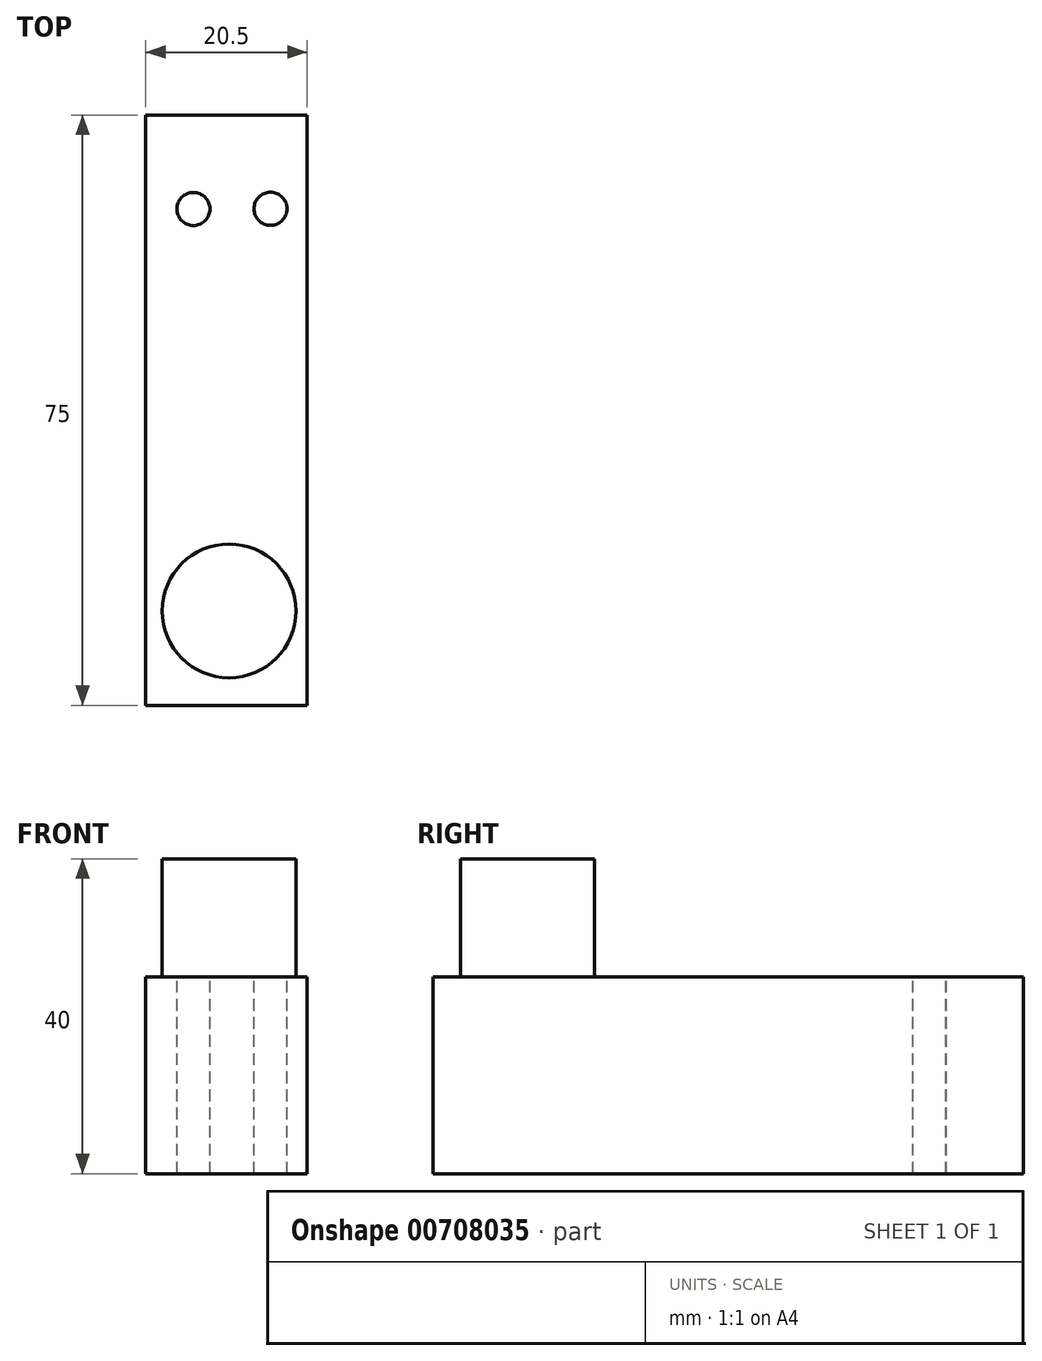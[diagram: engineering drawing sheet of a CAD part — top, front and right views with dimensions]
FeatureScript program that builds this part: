
annotation { "Feature Type Name" : "Feature", "Feature Type Description" : "" }
export const myFeature = defineFeature(function(context is Context, id is Id, definition is map)
    precondition{}
    {
        {
            var Q0;
            Q0=qCreatedBy(makeId("Top.planeOp"),FACE);
            var sketch = newSketch(context, id + "F0", { "sketchPlane" : qUnion([Q0])});
            skLineSegment(sketch, "E0.bottom", {"start": v(-10.6, 51.98) * mm, "end": v(9.9, 51.98) * mm});
            skLineSegment(sketch, "E0.top", {"start": v(-10.6, -23.02) * mm, "end": v(9.9, -23.02) * mm});
            skLineSegment(sketch, "E0.left", {"start": v(-10.6, 51.98) * mm, "end": v(-10.6, -23.02) * mm});
            skLineSegment(sketch, "E0.right", {"start": v(9.9, 51.98) * mm, "end": v(9.9, -23.02) * mm});
            skSolve(sketch);
        }
        {
            var Q0;
            Q0 = qSketchRegion(id + "F0", true);
            extrude(context, id + "F1", {"entities" : qUnion([Q0]), "depth" : 25 * mm, "offsetDistance" : 25 * mm});
        }
        {
            var Q0;
            Q0=makeQuery(id+"F1.opExtrude","CAP_FACE",FACE,{"disambiguationData":[OSD([sQuery(id+"F0.wireOp",EDGE,"E0.bottom"),sQuery(id+"F0.wireOp",EDGE,"E0.top"),sQuery(id+"F0.wireOp",EDGE,"E0.left"),sQuery(id+"F0.wireOp",EDGE,"E0.right")])],"isStart":false});
            var sketch = newSketch(context, id + "F2", { "sketchPlane" : qUnion([Q0])});
            skCircle(sketch, "E1", {"center": v(0, -11.02) * mm, "radius": 8.5 * mm});
            skSolve(sketch);
        }
        {
            var Q0;
            Q0 = qSketchRegion(id + "F2", true);
            extrude(context, id + "F3", {"entities" : qUnion([Q0]), "operationType" : NewBodyOperationType.ADD, "depth" : 15 * mm, "offsetDistance" : 25 * mm});
        }
        {
            var Q0;
            Q0=makeQuery(id+"F1.opExtrude","CAP_FACE",FACE,{"disambiguationData":[OSD([sQuery(id+"F0.wireOp",EDGE,"E0.bottom"),sQuery(id+"F0.wireOp",EDGE,"E0.top"),sQuery(id+"F0.wireOp",EDGE,"E0.left"),sQuery(id+"F0.wireOp",EDGE,"E0.right")])],"isStart":false});
            var sketch = newSketch(context, id + "F4", { "sketchPlane" : qUnion([Q0])});
            skCircle(sketch, "E2", {"center": v(-4.53, 40.03) * mm, "radius": 2.5 * mm});
            skCircle(sketch, "E3", {"center": v(5.27, 40.06) * mm, "radius": 2.37 * mm});
            skSolve(sketch);
        }
        {
            var Q0;
            Q0=sQuery(id+"F4.wireOp",VERTEX,"E2.center");
            var Q1;
            Q1=sQuery(id+"F4.wireOp",VERTEX,"E3.center");
            var Q2;
            Q2=makeQuery(id+"F1.opExtrude","SWEPT_BODY",BODY,{"disambiguationData":[OSD([sQuery(id+"F0.wireOp",EDGE,"E0.bottom"),sQuery(id+"F0.wireOp",EDGE,"E0.top"),sQuery(id+"F0.wireOp",EDGE,"E0.left"),sQuery(id+"F0.wireOp",EDGE,"E0.right")])]});
            hole(context, id + "F5", {"style" : HoleStyle.SIMPLE, "endStyle" : HoleEndStyle.THROUGH, "standardTappedOrClearance" : lookupTablePath({ "standard" : "ISO", "engagement" : "75%", "pitch" : "0.8 mm", "size" : "M5", "type" : "Tapped" }), "standardBlindInLast" : lookupTablePath({ "standard" : "ISO", "engagement" : "75%", "pitch" : "0.8 mm", "size" : "M5", "type" : "Tapped" }), "holeDiameter" : 4.2 * mm, "majorDiameter" : 5 * mm, "showTappedDepth" : true, "isTappedThrough" : true, "tappedDepth" : 12 * mm, "tapClearance" : 3, "locations" : qUnion([Q0, Q1]), "scope" : qUnion([Q2])});
        }
    });
